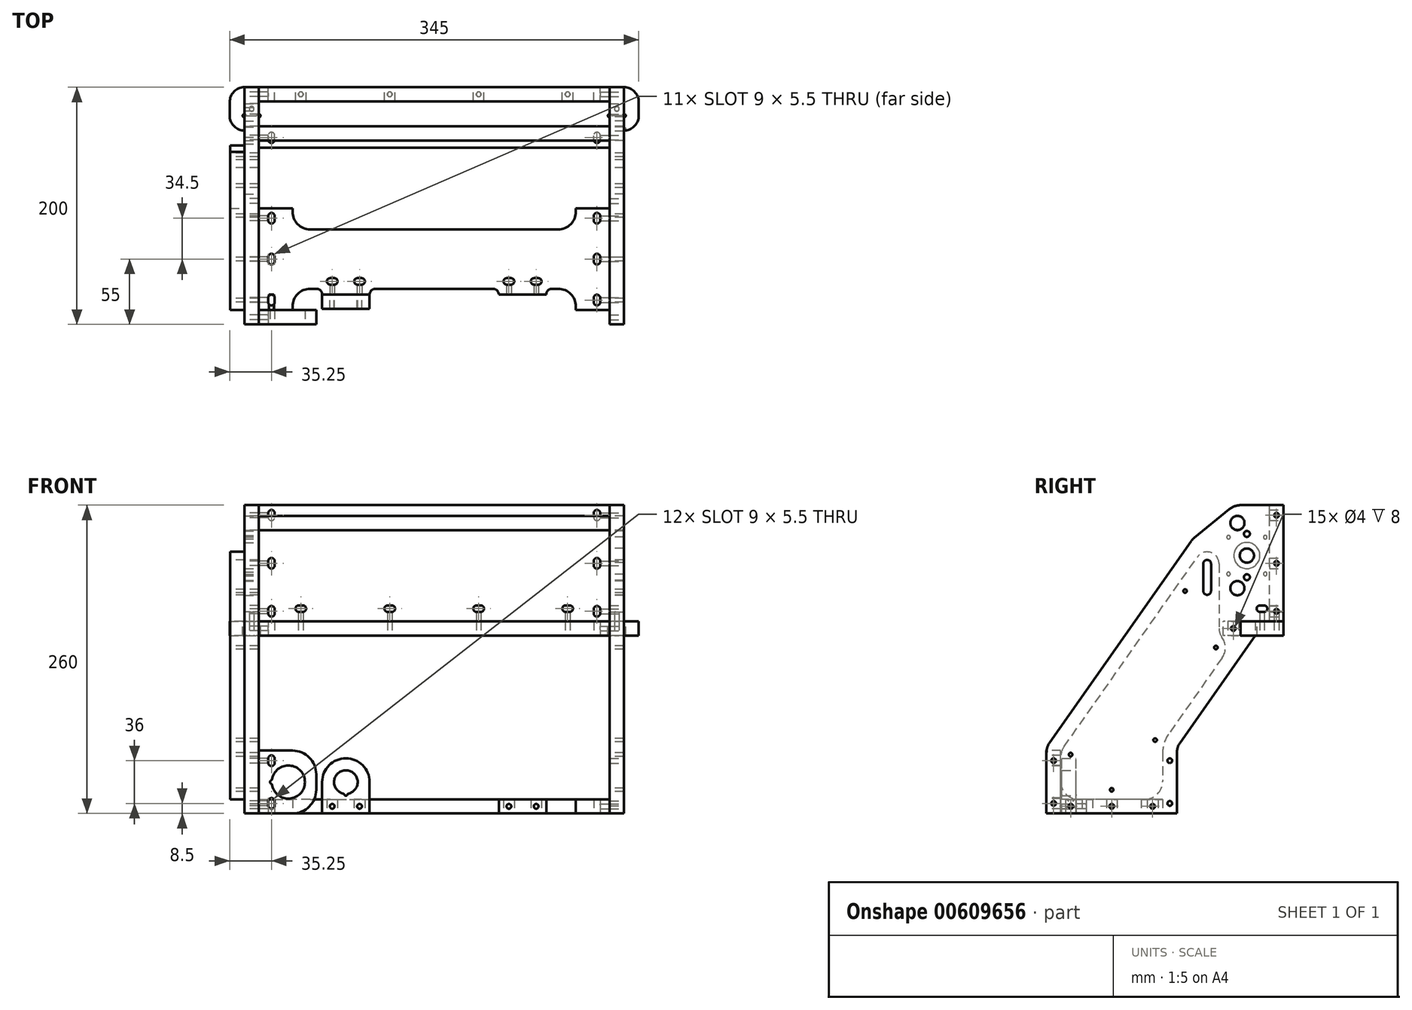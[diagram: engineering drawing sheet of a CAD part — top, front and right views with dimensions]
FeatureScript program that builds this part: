
annotation { "Feature Type Name" : "Feature", "Feature Type Description" : "" }
export const myFeature = defineFeature(function(context is Context, id is Id, definition is map)
    precondition{}
    {
        {
            var Q0;
            Q0=qCreatedBy(makeId("Front.planeOp"),FACE);
            var sketch = newSketch(context, id + "F0", { "sketchPlane" : qUnion([Q0])});
            skLineSegment(sketch, "E0.bottom", {"start": v(-148, 0) * mm, "end": v(148, 0) * mm});
            skLineSegment(sketch, "E0.top", {"start": v(-148, 98) * mm, "end": v(148, 98) * mm});
            skLineSegment(sketch, "E0.left", {"start": v(-148, 0) * mm, "end": v(-148, 98) * mm});
            skLineSegment(sketch, "E0.right", {"start": v(148, 0) * mm, "end": v(148, 98) * mm});
            skSolve(sketch);
        }
        {
            var Q0;
            Q0=qSketchRegion(id+"F0",true);
            extrude(context, id + "F1", {"entities" : qUnion([Q0]), "depth" : 12 * mm, "offsetDistance" : 25 * mm});
        }
        {
            var Q0;
            Q0=makeQuery(id+"F1.opExtrude","SWEPT_FACE",FACE,{"disambiguationData":[OSD([sQuery(id+"F0.wireOp",EDGE,"E0.left")])]});
            var sketch = newSketch(context, id + "F2", { "sketchPlane" : qUnion([Q0])});
            skLineSegment(sketch, "E1.bottom", {"start": v(0, 98) * mm, "end": v(56.7, 98) * mm});
            skLineSegment(sketch, "E1.top", {"start": v(90, -162) * mm, "end": v(200, -162) * mm});
            skLineSegment(sketch, "E1.right", {"start": v(56.7, 98) * mm, "end": v(200, -105.92) * mm});
            skLineSegment(sketch, "E2", {"start": v(200, -162) * mm, "end": v(200, -105.92) * mm});
            skLineSegment(sketch, "E3", {"start": v(24, -12) * mm, "end": v(90, -105.92) * mm});
            skLineSegment(sketch, "E4", {"start": v(0, 0) * mm, "end": v(0, 98) * mm});
            skLineSegment(sketch, "E5", {"start": v(90, -162) * mm, "end": v(90, -105.92) * mm});
            skLineSegment(sketch, "E6", {"start": v(0, 0) * mm, "end": v(24, 0) * mm});
            skLineSegment(sketch, "E7", {"start": v(24, 0) * mm, "end": v(24, -12) * mm});
            skSolve(sketch);
        }
        {
            var Q0;
            Q0=qSketchRegion(id+"F2",true);
            extrude(context, id + "F3", {"entities" : qUnion([Q0]), "depth" : 12 * mm, "offsetDistance" : 25 * mm});
        }
        {
            var Q0;
            Q0=makeQuery(id+"F3.opExtrude","CAP_FACE",FACE,{"disambiguationData":[OSD([sQuery(id+"F2.wireOp",EDGE,"E1.bottom"),sQuery(id+"F2.wireOp",EDGE,"E1.top"),sQuery(id+"F2.wireOp",EDGE,"E1.left"),sQuery(id+"F2.wireOp",EDGE,"E1.right"),sQuery(id+"F2.wireOp",EDGE,"E2"),sQuery(id+"F2.wireOp",EDGE,"2146645f-f5f1-4766-9391-dd441536dbd0.filletArc"),sQuery(id+"F2.wireOp",EDGE,"94e26631-0c9e-45e8-bca5-160914bd0a3d.filletArc")])],"isStart":true});
            var sketch = newSketch(context, id + "F4", { "sketchPlane" : qUnion([Q0])});
            skCircle(sketch, "E8", {"center": v(-39, 28) * mm, "radius": 5.97 * mm});
            skCircle(sketch, "E9", {"center": v(-39, 83) * mm, "radius": 5.97 * mm});
            skLineSegment(sketch, "E10", {"start": v(-39, 28) * mm, "end": v(-39, 83) * mm, "construction": true});
            skCircle(sketch, "E11", {"center": v(-31, 55.5) * mm, "radius": 11 * mm});
            skPoint(sketch, "E11.centerSnap0", {"position": v(-39, 55.5) * mm});
            skLineSegment(sketch, "E12.bottom", {"start": v(-15.5, 71) * mm, "end": v(-46.5, 71) * mm, "construction": true});
            skLineSegment(sketch, "E12.top", {"start": v(-15.5, 40) * mm, "end": v(-46.5, 40) * mm, "construction": true});
            skLineSegment(sketch, "E12.left", {"start": v(-15.5, 71) * mm, "end": v(-15.5, 40) * mm, "construction": true});
            skLineSegment(sketch, "E12.right", {"start": v(-46.5, 71) * mm, "end": v(-46.5, 40) * mm, "construction": true});
            skLineSegment(sketch, "E13", {"start": v(-31, 55.5) * mm, "end": v(-31, 71) * mm, "construction": true});
            skLineSegment(sketch, "E14", {"start": v(-15.5, 55.5) * mm, "end": v(-31, 55.5) * mm, "construction": true});
            skCircle(sketch, "E15", {"center": v(-46.5, 71) * mm, "radius": 1.5 * mm});
            skCircle(sketch, "E16.1.0", {"center": v(-46.5, 40) * mm, "radius": 1.5 * mm});
            skCircle(sketch, "E16.2.0", {"center": v(-15.5, 40) * mm, "radius": 1.5 * mm});
            skCircle(sketch, "E16.3.0", {"center": v(-15.5, 71) * mm, "radius": 1.5 * mm});
            skCircle(sketch, "E17", {"center": v(-31, 73.75) * mm, "radius": 2.5 * mm});
            skCircle(sketch, "E18.MirrorC", {"center": v(-31, 37.25) * mm, "radius": 2.5 * mm});
            skSolve(sketch);
        }
        {
            var Q0;
            Q0=qSketchRegion(id+"F4",true);
            extrude(context, id + "F5", {"entities" : qUnion([Q0]), "operationType" : NewBodyOperationType.REMOVE, "oppositeDirection" : true, "depth" : 25 * mm, "offsetDistance" : 25 * mm});
        }
        {
            var Q0;
            Q0=makeQuery(id+"F3.opExtrude","CAP_FACE",FACE,{"disambiguationData":[OSD([sQuery(id+"F2.wireOp",EDGE,"E1.bottom"),sQuery(id+"F2.wireOp",EDGE,"E1.top"),sQuery(id+"F2.wireOp",EDGE,"E1.left"),sQuery(id+"F2.wireOp",EDGE,"E1.right"),sQuery(id+"F2.wireOp",EDGE,"E2"),sQuery(id+"F2.wireOp",EDGE,"2146645f-f5f1-4766-9391-dd441536dbd0.filletArc"),sQuery(id+"F2.wireOp",EDGE,"94e26631-0c9e-45e8-bca5-160914bd0a3d.filletArc")])],"isStart":false});
            var sketch = newSketch(context, id + "F6", { "sketchPlane" : qUnion([Q0])});
            skCircle(sketch, "E19", {"center": v(39, 83) * mm, "radius": 6 * mm});
            skSolve(sketch);
        }
        {
            var Q0;
            Q0=qSketchRegion(id+"F6",true);
            extrude(context, id + "F7", {"entities" : qUnion([Q0]), "oppositeDirection" : true, "depth" : 320 * mm, "offsetDistance" : 25 * mm});
        }
        {
            var Q0;
            Q0=makeQuery(id+"F1.opExtrude","SWEPT_FACE",FACE,{"disambiguationData":[OSD([sQuery(id+"F0.wireOp",EDGE,"E0.right")])]});
            var sketch = newSketch(context, id + "F8", { "sketchPlane" : qUnion([Q0])});
            skCircle(sketch, "E20.0", {"center": v(-39, 83) * mm, "radius": 5.97 * mm});
            skCircle(sketch, "E21.0", {"center": v(-39, 28) * mm, "radius": 5.97 * mm});
            skLineSegment(sketch, "E22.1", {"start": v(-90, -105.92) * mm, "end": v(-24, -12) * mm});
            skLineSegment(sketch, "E22.5", {"start": v(0, 98) * mm, "end": v(-56.7, 98) * mm});
            skLineSegment(sketch, "E22.6", {"start": v(-56.7, 98) * mm, "end": v(-200, -105.92) * mm});
            skLineSegment(sketch, "E22.8", {"start": v(0, 0) * mm, "end": v(0, 98) * mm});
            skLineSegment(sketch, "E22.9", {"start": v(-200, -105.92) * mm, "end": v(-200, -162) * mm});
            skLineSegment(sketch, "E22.10", {"start": v(-200, -162) * mm, "end": v(-90, -162) * mm});
            skLineSegment(sketch, "E22.11", {"start": v(-90, -162) * mm, "end": v(-90, -105.92) * mm});
            skCircle(sketch, "E23.0", {"center": v(-31, 73.75) * mm, "radius": 2.5 * mm});
            skCircle(sketch, "E24.0", {"center": v(-31, 37.25) * mm, "radius": 2.5 * mm});
            skCircle(sketch, "E25.0", {"center": v(-31, 55.5) * mm, "radius": 6 * mm});
            skLineSegment(sketch, "E26", {"start": v(-24, -12) * mm, "end": v(-24, 0) * mm});
            skLineSegment(sketch, "E27", {"start": v(-24, 0) * mm, "end": v(0, 0) * mm});
            skSolve(sketch);
        }
        {
            var Q0;
            Q0=qSketchRegion(id+"F8",true);
            extrude(context, id + "F9", {"entities" : qUnion([Q0]), "depth" : 12 * mm, "offsetDistance" : 25 * mm});
        }
        {
            var Q0;
            Q0=makeQuery(id+"F3.opExtrude","SWEPT_FACE",FACE,{"disambiguationData":[OSD([sQuery(id+"F2.wireOp",EDGE,"E2")])]});
            var sketch = newSketch(context, id + "F10", { "sketchPlane" : qUnion([Q0])});
            skLineSegment(sketch, "E28.bottom", {"start": v(-148, -162) * mm, "end": v(-119.5, -162) * mm});
            skLineSegment(sketch, "E28.top", {"start": v(-148, -109) * mm, "end": v(-119.5, -109) * mm});
            skLineSegment(sketch, "E28.left", {"start": v(-148, -162) * mm, "end": v(-148, -109) * mm});
            skLineSegment(sketch, "E28.right", {"start": v(-99.5, -142) * mm, "end": v(-99.5, -129) * mm});
            skArc(sketch, "E29", {"start": v(-136.8, -137.7) * mm, "mid": v(-109.02, -135.5) * mm, "end": v(-136.8, -133.3) * mm});
            skPoint(sketch, "E29.centerSnap0", {"position": v(-148, -135.5) * mm});
            skPoint(sketch, "E29.centerSnap1", {"position": v(-123, -160.5) * mm});
            skArc(sketch, "E30.filletArc", {"start": v(-99.5, -129) * mm, "mid": v(-105.36, -114.86) * mm, "end": v(-119.5, -109) * mm});
            skArc(sketch, "E31.filletArc", {"start": v(-119.5, -162) * mm, "mid": v(-105.36, -156.14) * mm, "end": v(-99.5, -142) * mm});
            skArc(sketch, "E32", {"start": v(-137.46, -134.08) * mm, "mid": v(-138.47, -135.5) * mm, "end": v(-137.46, -136.92) * mm});
            skPoint(sketch, "E33.visualSharp", {"position": v(-136.9, -134) * mm});
            skArc(sketch, "E33.filletArc", {"start": v(-137.46, -134.08) * mm, "mid": v(-137.02, -133.78) * mm, "end": v(-136.8, -133.3) * mm});
            skPoint(sketch, "E34.visualSharp", {"position": v(-136.9, -137) * mm});
            skArc(sketch, "E34.filletArc", {"start": v(-136.8, -137.7) * mm, "mid": v(-137.02, -137.22) * mm, "end": v(-137.46, -136.92) * mm});
            skSolve(sketch);
        }
        {
            var Q0;
            Q0=qSketchRegion(id+"F10",true);
            extrude(context, id + "F11", {"entities" : qUnion([Q0]), "oppositeDirection" : true, "depth" : 12 * mm, "offsetDistance" : 25 * mm});
        }
        {
            var Q0;
            Q0=makeQuery(id+"F3.opExtrude","SWEPT_FACE",FACE,{"disambiguationData":[OSD([sQuery(id+"F2.wireOp",EDGE,"E1.top")])]});
            var sketch = newSketch(context, id + "F12", { "sketchPlane" : qUnion([Q0])});
            skLineSegment(sketch, "E35.bottom", {"start": v(-104.5, 170) * mm, "end": v(-99.5, 170) * mm});
            skLineSegment(sketch, "E35.top", {"start": v(-148, 145) * mm, "end": v(148, 145) * mm, "construction": true});
            skLineSegment(sketch, "E36.top", {"start": v(-148, 188) * mm, "end": v(-119.5, 188) * mm});
            skPoint(sketch, "E37", {"position": v(-148, 145) * mm});
            skLineSegment(sketch, "E38.trimOffspring", {"start": v(-119.5, 185) * mm, "end": v(-119.5, 188) * mm});
            skPoint(sketch, "E39.visualSharp", {"position": v(-119.5, 170) * mm});
            skArc(sketch, "E39.filletArc", {"start": v(-119.5, 185) * mm, "mid": v(-115.1, 174.4) * mm, "end": v(-104.5, 170) * mm});
            skLineSegment(sketch, "E40", {"start": v(-148, 188) * mm, "end": v(-148, 145) * mm});
            skLineSegment(sketch, "E41", {"start": v(0, 145) * mm, "end": v(0, 170) * mm, "construction": true});
            skLineSegment(sketch, "E42.MirrorCS", {"start": v(104.5, 170) * mm, "end": v(99.5, 170) * mm});
            skArc(sketch, "E43.MirrorCS", {"start": v(119.5, 185) * mm, "mid": v(115.1, 174.4) * mm, "end": v(104.5, 170) * mm});
            skLineSegment(sketch, "E44.MirrorCS", {"start": v(119.5, 185) * mm, "end": v(119.5, 188) * mm});
            skLineSegment(sketch, "E45.MirrorCS", {"start": v(148, 188) * mm, "end": v(119.5, 188) * mm});
            skLineSegment(sketch, "E46.MirrorCS", {"start": v(148, 188) * mm, "end": v(148, 145) * mm});
            skLineSegment(sketch, "E47.MirrorCS", {"start": v(-119.5, 105) * mm, "end": v(-119.5, 102) * mm});
            skLineSegment(sketch, "E48.MirrorCS", {"start": v(119.5, 105) * mm, "end": v(119.5, 102) * mm});
            skLineSegment(sketch, "E49.MirrorCS", {"start": v(-148, 102) * mm, "end": v(-119.5, 102) * mm});
            skLineSegment(sketch, "E50.MirrorCS", {"start": v(148, 102) * mm, "end": v(119.5, 102) * mm});
            skLineSegment(sketch, "E51.MirrorCS", {"start": v(148, 102) * mm, "end": v(148, 145) * mm});
            skLineSegment(sketch, "E52.MirrorCS", {"start": v(-104.5, 120) * mm, "end": v(0, 120) * mm});
            skArc(sketch, "E53.MirrorCS", {"start": v(119.5, 105) * mm, "mid": v(115.1, 115.6) * mm, "end": v(104.5, 120) * mm});
            skLineSegment(sketch, "E54.MirrorCS", {"start": v(104.5, 120) * mm, "end": v(0, 120) * mm});
            skPoint(sketch, "E55.MirrorP", {"position": v(-119.5, 120) * mm});
            skArc(sketch, "E56.MirrorCS", {"start": v(-119.5, 105) * mm, "mid": v(-115.1, 115.6) * mm, "end": v(-104.5, 120) * mm});
            skLineSegment(sketch, "E57.MirrorCS", {"start": v(-148, 102) * mm, "end": v(-148, 145) * mm});
            skLineSegment(sketch, "E58", {"start": v(-137.25, 108.75) * mm, "end": v(-137.25, 112.25) * mm, "construction": true});
            skArc(sketch, "E59.0.startCap", {"start": v(-134.5, 108.75) * mm, "mid": v(-137.25, 106) * mm, "end": v(-140, 108.75) * mm});
            skArc(sketch, "E59.0.endCap", {"start": v(-140, 112.25) * mm, "mid": v(-137.25, 115) * mm, "end": v(-134.5, 112.25) * mm});
            skLineSegment(sketch, "E59.0.left", {"start": v(-140, 108.75) * mm, "end": v(-140, 112.25) * mm});
            skLineSegment(sketch, "E59.0.right", {"start": v(-134.5, 108.75) * mm, "end": v(-134.5, 112.25) * mm});
            skArc(sketch, "E60.MirrorCS", {"start": v(-140, 177.75) * mm, "mid": v(-137.25, 175) * mm, "end": v(-134.5, 177.75) * mm});
            skLineSegment(sketch, "E61.MirrorCS", {"start": v(-134.5, 181.25) * mm, "end": v(-134.5, 177.75) * mm});
            skArc(sketch, "E62.MirrorCS", {"start": v(-140, 181.25) * mm, "mid": v(-137.25, 184) * mm, "end": v(-134.5, 181.25) * mm});
            skLineSegment(sketch, "E63.MirrorCS", {"start": v(-140, 181.25) * mm, "end": v(-140, 177.75) * mm});
            skLineSegment(sketch, "E64", {"start": v(-137.25, 143.25) * mm, "end": v(-137.25, 146.75) * mm, "construction": true});
            skArc(sketch, "E65.0.startCap", {"start": v(-134.5, 143.25) * mm, "mid": v(-137.25, 140.5) * mm, "end": v(-140, 143.25) * mm});
            skArc(sketch, "E65.0.endCap", {"start": v(-140, 146.75) * mm, "mid": v(-137.25, 149.5) * mm, "end": v(-134.5, 146.75) * mm});
            skLineSegment(sketch, "E65.0.left", {"start": v(-140, 143.25) * mm, "end": v(-140, 146.75) * mm});
            skLineSegment(sketch, "E65.0.right", {"start": v(-134.5, 143.25) * mm, "end": v(-134.5, 146.75) * mm});
            skPoint(sketch, "E66", {"position": v(-137.25, 145) * mm});
            skLineSegment(sketch, "E67.MirrorCS", {"start": v(137.25, 108.75) * mm, "end": v(137.25, 112.25) * mm, "construction": true});
            skLineSegment(sketch, "E68.MirrorCS", {"start": v(137.25, 143.25) * mm, "end": v(137.25, 146.75) * mm, "construction": true});
            skLineSegment(sketch, "E69.MirrorCS", {"start": v(134.5, 108.75) * mm, "end": v(134.5, 112.25) * mm});
            skPoint(sketch, "E70.MirrorP", {"position": v(137.25, 145) * mm});
            skLineSegment(sketch, "E71.MirrorCS", {"start": v(140, 181.25) * mm, "end": v(140, 177.75) * mm});
            skLineSegment(sketch, "E72.MirrorCS", {"start": v(140, 143.25) * mm, "end": v(140, 146.75) * mm});
            skLineSegment(sketch, "E73.MirrorCS", {"start": v(134.5, 181.25) * mm, "end": v(134.5, 177.75) * mm});
            skLineSegment(sketch, "E74.MirrorCS", {"start": v(140, 108.75) * mm, "end": v(140, 112.25) * mm});
            skLineSegment(sketch, "E75.MirrorCS", {"start": v(134.5, 143.25) * mm, "end": v(134.5, 146.75) * mm});
            skArc(sketch, "E76.MirrorCS", {"start": v(140, 112.25) * mm, "mid": v(137.25, 115) * mm, "end": v(134.5, 112.25) * mm});
            skArc(sketch, "E77.MirrorCS", {"start": v(140, 181.25) * mm, "mid": v(137.25, 184) * mm, "end": v(134.5, 181.25) * mm});
            skArc(sketch, "E78.MirrorCS", {"start": v(134.5, 108.75) * mm, "mid": v(137.25, 106) * mm, "end": v(140, 108.75) * mm});
            skArc(sketch, "E79.MirrorCS", {"start": v(140, 146.75) * mm, "mid": v(137.25, 149.5) * mm, "end": v(134.5, 146.75) * mm});
            skPoint(sketch, "E80.MirrorP", {"position": v(119.5, 120) * mm});
            skArc(sketch, "E81.MirrorCS", {"start": v(140, 177.75) * mm, "mid": v(137.25, 175) * mm, "end": v(134.5, 177.75) * mm});
            skPoint(sketch, "E82.MirrorP", {"position": v(119.5, 170) * mm});
            skArc(sketch, "E83.MirrorCS", {"start": v(134.5, 143.25) * mm, "mid": v(137.25, 140.5) * mm, "end": v(140, 143.25) * mm});
            skLineSegment(sketch, "E84", {"start": v(-94.5, 175) * mm, "end": v(-54.5, 175) * mm});
            skArc(sketch, "E85", {"start": v(-99.5, 170) * mm, "mid": v(-95.96, 171.46) * mm, "end": v(-94.5, 175) * mm});
            skPoint(sketch, "E86.orphan", {"position": v(0, 170) * mm});
            skArc(sketch, "E87.MirrorCS", {"start": v(-49.5, 170) * mm, "mid": v(-53.04, 171.46) * mm, "end": v(-54.5, 175) * mm});
            skLineSegment(sketch, "E88", {"start": v(-49.5, 170) * mm, "end": v(0, 170) * mm});
            skLineSegment(sketch, "E89.MirrorCS", {"start": v(49.5, 170) * mm, "end": v(0, 170) * mm});
            skArc(sketch, "E90.MirrorCS", {"start": v(49.5, 170) * mm, "mid": v(53.04, 171.46) * mm, "end": v(54.5, 175) * mm});
            skLineSegment(sketch, "E91.MirrorCS", {"start": v(94.5, 175) * mm, "end": v(54.5, 175) * mm});
            skArc(sketch, "E92.MirrorCS", {"start": v(99.5, 170) * mm, "mid": v(95.96, 171.46) * mm, "end": v(94.5, 175) * mm});
            skLineSegment(sketch, "E93", {"start": v(-87.75, 163.75) * mm, "end": v(-84.25, 163.75) * mm, "construction": true});
            skArc(sketch, "E94.0.startCap", {"start": v(-87.75, 161) * mm, "mid": v(-90.5, 163.75) * mm, "end": v(-87.75, 166.5) * mm});
            skArc(sketch, "E94.0.endCap", {"start": v(-84.25, 166.5) * mm, "mid": v(-81.5, 163.75) * mm, "end": v(-84.25, 161) * mm});
            skLineSegment(sketch, "E94.0.left", {"start": v(-87.75, 166.5) * mm, "end": v(-84.25, 166.5) * mm});
            skLineSegment(sketch, "E94.0.right", {"start": v(-87.75, 161) * mm, "end": v(-84.25, 161) * mm});
            skLineSegment(sketch, "E95", {"start": v(-94.5, 175) * mm, "end": v(-94.5, 170) * mm, "construction": true});
            skLineSegment(sketch, "E96", {"start": v(-74.5, 175) * mm, "end": v(-74.5, 172.2) * mm, "construction": true});
            skArc(sketch, "E97.MirrorCS", {"start": v(-64.75, 166.5) * mm, "mid": v(-67.5, 163.75) * mm, "end": v(-64.75, 161) * mm});
            skLineSegment(sketch, "E98.MirrorCS", {"start": v(-61.25, 161) * mm, "end": v(-64.75, 161) * mm});
            skLineSegment(sketch, "E99.MirrorCS", {"start": v(-61.25, 166.5) * mm, "end": v(-64.75, 166.5) * mm});
            skArc(sketch, "E100.MirrorCS", {"start": v(-61.25, 161) * mm, "mid": v(-58.5, 163.75) * mm, "end": v(-61.25, 166.5) * mm});
            skLineSegment(sketch, "E101.MirrorCS", {"start": v(61.25, 166.5) * mm, "end": v(64.75, 166.5) * mm});
            skLineSegment(sketch, "E102.MirrorCS", {"start": v(87.75, 166.5) * mm, "end": v(84.25, 166.5) * mm});
            skArc(sketch, "E103.MirrorCS", {"start": v(61.25, 161) * mm, "mid": v(58.5, 163.75) * mm, "end": v(61.25, 166.5) * mm});
            skLineSegment(sketch, "E104.MirrorCS", {"start": v(61.25, 161) * mm, "end": v(64.75, 161) * mm});
            skArc(sketch, "E105.MirrorCS", {"start": v(64.75, 166.5) * mm, "mid": v(67.5, 163.75) * mm, "end": v(64.75, 161) * mm});
            skArc(sketch, "E106.MirrorCS", {"start": v(84.25, 166.5) * mm, "mid": v(81.5, 163.75) * mm, "end": v(84.25, 161) * mm});
            skLineSegment(sketch, "E107.MirrorCS", {"start": v(87.75, 161) * mm, "end": v(84.25, 161) * mm});
            skArc(sketch, "E108.MirrorCS", {"start": v(87.75, 161) * mm, "mid": v(90.5, 163.75) * mm, "end": v(87.75, 166.5) * mm});
            skSolve(sketch);
        }
        {
            var Q0;
            Q0=qSketchRegion(id+"F12",true);
            extrude(context, id + "F13", {"entities" : qUnion([Q0]), "oppositeDirection" : true, "depth" : 12 * mm, "offsetDistance" : 25 * mm});
        }
        {
            var Q0;
            Q0=makeQuery(id+"F11.opExtrude","CAP_FACE",FACE,{"disambiguationData":[OSD([sQuery(id+"F10.wireOp",EDGE,"E28.bottom"),sQuery(id+"F10.wireOp",EDGE,"E28.top"),sQuery(id+"F10.wireOp",EDGE,"E28.left"),sQuery(id+"F10.wireOp",EDGE,"E28.right"),sQuery(id+"F10.wireOp",EDGE,"E29"),sQuery(id+"F10.wireOp",EDGE,"E30.filletArc"),sQuery(id+"F10.wireOp",EDGE,"E31.filletArc")])],"isStart":true});
            var sketch = newSketch(context, id + "F14", { "sketchPlane" : qUnion([Q0])});
            skLineSegment(sketch, "E109", {"start": v(-137.25, -115.75) * mm, "end": v(-137.25, -119.25) * mm, "construction": true});
            skArc(sketch, "E110.0.startCap", {"start": v(-140, -115.75) * mm, "mid": v(-137.25, -113) * mm, "end": v(-134.5, -115.75) * mm});
            skArc(sketch, "E110.0.endCap", {"start": v(-134.5, -119.25) * mm, "mid": v(-137.25, -122) * mm, "end": v(-140, -119.25) * mm});
            skLineSegment(sketch, "E110.0.left", {"start": v(-134.5, -115.75) * mm, "end": v(-134.5, -119.25) * mm});
            skLineSegment(sketch, "E110.0.right", {"start": v(-140, -115.75) * mm, "end": v(-140, -119.25) * mm});
            skLineSegment(sketch, "E111", {"start": v(-148, -135.5) * mm, "end": v(-136.97, -135.5) * mm, "construction": true});
            skLineSegment(sketch, "E112.MirrorCS", {"start": v(-134.5, -155.25) * mm, "end": v(-134.5, -151.75) * mm});
            skLineSegment(sketch, "E113.MirrorCS", {"start": v(-140, -155.25) * mm, "end": v(-140, -151.75) * mm});
            skArc(sketch, "E114.MirrorCS", {"start": v(-140, -155.25) * mm, "mid": v(-137.25, -158) * mm, "end": v(-134.5, -155.25) * mm});
            skArc(sketch, "E115.MirrorCS", {"start": v(-134.5, -151.75) * mm, "mid": v(-137.25, -149) * mm, "end": v(-140, -151.75) * mm});
            skSolve(sketch);
        }
        {
            var Q0;
            Q0 = qSketchRegion(id + "F14", true);
            extrude(context, id + "F15", {"entities" : qUnion([Q0]), "operationType" : NewBodyOperationType.REMOVE, "oppositeDirection" : true, "depth" : 25 * mm, "offsetDistance" : 25 * mm});
        }
        {
            var Q0;
            Q0=makeQuery(id+"F1.opExtrude","SWEPT_FACE",FACE,{"disambiguationData":[OSD([sQuery(id+"F0.wireOp",EDGE,"E0.bottom")])]});
            var sketch = newSketch(context, id + "F16", { "sketchPlane" : qUnion([Q0])});
            skLineSegment(sketch, "E116", {"start": v(-160, 0) * mm, "end": v(160, 0) * mm});
            skLineSegment(sketch, "E117", {"start": v(-160, 0) * mm, "end": v(-160, 12.5) * mm});
            skLineSegment(sketch, "E118", {"start": v(-157.7, 24) * mm, "end": v(-150.3, 24) * mm});
            skLineSegment(sketch, "E119", {"start": v(-148, 26.3) * mm, "end": v(-148, 51) * mm});
            skLineSegment(sketch, "E120", {"start": v(-148, 51) * mm, "end": v(0, 51) * mm});
            skLineSegment(sketch, "E121", {"start": v(0, 51) * mm, "end": v(0, 0) * mm, "construction": true});
            skArc(sketch, "E122", {"start": v(-149.37, 23.4) * mm, "mid": v(-146.94, 22.94) * mm, "end": v(-147.4, 25.37) * mm});
            skArc(sketch, "E123.MirrorC", {"start": v(149.37, 23.4) * mm, "mid": v(146.94, 22.94) * mm, "end": v(147.4, 25.37) * mm});
            skLineSegment(sketch, "E124.MirrorCS", {"start": v(148, 51) * mm, "end": v(0, 51) * mm});
            skLineSegment(sketch, "E125.MirrorCS", {"start": v(148, 26.3) * mm, "end": v(148, 51) * mm});
            skLineSegment(sketch, "E126.MirrorCS", {"start": v(158.5, 24) * mm, "end": v(150.3, 24) * mm});
            skLineSegment(sketch, "E127.MirrorCS", {"start": v(160, 0) * mm, "end": v(160, 22.5) * mm});
            skPoint(sketch, "E128.visualSharp", {"position": v(149.5, 24) * mm});
            skArc(sketch, "E128.filletArc", {"start": v(150.3, 24) * mm, "mid": v(149.74, 23.84) * mm, "end": v(149.37, 23.4) * mm});
            skPoint(sketch, "E129.visualSharp", {"position": v(148, 25.5) * mm});
            skArc(sketch, "E129.filletArc", {"start": v(147.4, 25.37) * mm, "mid": v(147.84, 25.74) * mm, "end": v(148, 26.3) * mm});
            skPoint(sketch, "E130.visualSharp", {"position": v(-149.5, 24) * mm});
            skArc(sketch, "E130.filletArc", {"start": v(-149.37, 23.4) * mm, "mid": v(-149.74, 23.84) * mm, "end": v(-150.3, 24) * mm});
            skPoint(sketch, "E131.visualSharp", {"position": v(-148, 25.5) * mm});
            skArc(sketch, "E131.filletArc", {"start": v(-148, 26.3) * mm, "mid": v(-147.84, 25.74) * mm, "end": v(-147.4, 25.37) * mm});
            skArc(sketch, "E132", {"start": v(-161.16, 24.95) * mm, "mid": v(-172.49, 11.92) * mm, "end": v(-160, 0) * mm});
            skArc(sketch, "E133", {"start": v(-161.09, 36.45) * mm, "mid": v(-172.49, 23.46) * mm, "end": v(-160, 11.5) * mm});
            skLineSegment(sketch, "E134", {"start": v(-160, 26.3) * mm, "end": v(-160, 35.46) * mm});
            skArc(sketch, "E135", {"start": v(-160.6, 25.37) * mm, "mid": v(-161.06, 22.94) * mm, "end": v(-158.63, 23.4) * mm});
            skPoint(sketch, "E136.visualSharp", {"position": v(-160, 25.5) * mm});
            skArc(sketch, "E136.filletArc", {"start": v(-160.6, 25.37) * mm, "mid": v(-160.16, 25.74) * mm, "end": v(-160, 26.3) * mm});
            skPoint(sketch, "E137.visualSharp", {"position": v(-158.5, 24) * mm});
            skArc(sketch, "E137.filletArc", {"start": v(-157.7, 24) * mm, "mid": v(-158.26, 23.84) * mm, "end": v(-158.63, 23.4) * mm});
            skLineSegment(sketch, "E138", {"start": v(-172.5, 12.5) * mm, "end": v(-172.5, 24) * mm});
            skPoint(sketch, "E138.startSnap0", {"position": v(-172.5, 24) * mm});
            skPoint(sketch, "E139.visualSharp", {"position": v(-160, 36.5) * mm});
            skArc(sketch, "E139.filletArc", {"start": v(-160, 35.46) * mm, "mid": v(-160.32, 36.2) * mm, "end": v(-161.09, 36.45) * mm});
            skArc(sketch, "E140.MirrorCS", {"start": v(160.6, 25.37) * mm, "mid": v(160.16, 25.74) * mm, "end": v(160, 26.3) * mm});
            skArc(sketch, "E141.MirrorCS", {"start": v(160, 35.46) * mm, "mid": v(160.32, 36.2) * mm, "end": v(161.09, 36.45) * mm});
            skArc(sketch, "E142.MirrorCS", {"start": v(157.7, 24) * mm, "mid": v(158.26, 23.84) * mm, "end": v(158.63, 23.4) * mm});
            skArc(sketch, "E143.MirrorCS", {"start": v(160.6, 25.37) * mm, "mid": v(161.06, 22.94) * mm, "end": v(158.63, 23.4) * mm});
            skPoint(sketch, "E144.MirrorP", {"position": v(160, 36.5) * mm});
            skPoint(sketch, "E145.MirrorP", {"position": v(160, 25.5) * mm});
            skLineSegment(sketch, "E146.MirrorCS", {"start": v(172.5, 12.5) * mm, "end": v(172.5, 24) * mm});
            skArc(sketch, "E147.MirrorCS", {"start": v(161.09, 36.45) * mm, "mid": v(172.49, 23.46) * mm, "end": v(160, 11.5) * mm});
            skLineSegment(sketch, "E148.MirrorCS", {"start": v(160, 0) * mm, "end": v(160, 12.5) * mm});
            skLineSegment(sketch, "E149.MirrorCS", {"start": v(160, 26.3) * mm, "end": v(160, 35.46) * mm});
            skArc(sketch, "E150.MirrorCS", {"start": v(161.16, 24.95) * mm, "mid": v(172.49, 11.92) * mm, "end": v(160, 0) * mm});
            skPoint(sketch, "E151.MirrorP", {"position": v(172.5, 24) * mm});
            skPoint(sketch, "E152.MirrorP", {"position": v(158.5, 24) * mm});
            skSolve(sketch);
        }
        {
            var Q0;
            Q0 = qSketchRegion(id + "F16", true);
            extrude(context, id + "F17", {"entities" : qUnion([Q0]), "depth" : 12 * mm, "offsetDistance" : 25 * mm});
        }
        {
            var Q0;
            Q0=makeQuery(id+"F3.opExtrude","CAP_FACE",FACE,{"disambiguationData":[OSD([sQuery(id+"F2.wireOp",EDGE,"E1.bottom"),sQuery(id+"F2.wireOp",EDGE,"E1.top"),sQuery(id+"F2.wireOp",EDGE,"E1.right"),sQuery(id+"F2.wireOp",EDGE,"E2"),sQuery(id+"F2.wireOp",EDGE,"94e26631-0c9e-45e8-bca5-160914bd0a3d.filletArc"),sQuery(id+"F2.wireOp",EDGE,"E3"),sQuery(id+"F2.wireOp",EDGE,"E4"),sQuery(id+"F2.wireOp",EDGE,"3c304bfc-2885-443d-81d9-234e97ae9333.filletArc"),sQuery(id+"F2.wireOp",EDGE,"E5"),sQuery(id+"F2.wireOp",EDGE,"930fecb7-9af6-459d-8abb-d03ba6c7b7a5.filletArc"),sQuery(id+"F2.wireOp",EDGE,"yWCbbJBZ-1GEx-dhOH-k0kd-LSXJYkVx6NrP"),sQuery(id+"F2.wireOp",EDGE,"cebc93dc-49be-47df-9592-c98bafc6a396.filletArc"),sQuery(id+"F2.wireOp",EDGE,"0R2F742G-mTnw-hJEY-WdgB-tpz7tOERiha1"),sQuery(id+"F2.wireOp",EDGE,"3aeea579-ff88-4944-83f2-f3d4fbf2bd07.filletArc"),sQuery(id+"F2.wireOp",EDGE,"c7c51ab0-1a95-4586-bb57-7b3897809644.filletArc")])],"isStart":false});
            var sketch = newSketch(context, id + "F18", { "sketchPlane" : qUnion([Q0])});
            skCircle(sketch, "E153", {"center": v(194, -153.5) * mm, "radius": 2 * mm});
            skCircle(sketch, "E154", {"center": v(194, -117.5) * mm, "radius": 2 * mm});
            skLineSegment(sketch, "E155", {"start": v(145, -162) * mm, "end": v(145, -142.37) * mm, "construction": true});
            skCircle(sketch, "E156.MirrorC", {"center": v(96, -117.5) * mm, "radius": 2 * mm});
            skCircle(sketch, "E157.MirrorC", {"center": v(96, -153.5) * mm, "radius": 2 * mm});
            skCircle(sketch, "E158", {"center": v(179.5, -156) * mm, "radius": 2 * mm});
            skCircle(sketch, "E159", {"center": v(145, -156) * mm, "radius": 2 * mm});
            skCircle(sketch, "E160.MirrorC", {"center": v(110.5, -156) * mm, "radius": 2 * mm});
            skCircle(sketch, "E161", {"center": v(6, 89.5) * mm, "radius": 2 * mm});
            skCircle(sketch, "E162.0.1.0", {"center": v(6, 49) * mm, "radius": 2 * mm});
            skCircle(sketch, "E162.0.2.0", {"center": v(6, 8.5) * mm, "radius": 2 * mm});
            skLineSegment(sketch, "E162.direction1", {"start": v(6, 89.5) * mm, "end": v(31, 89.5) * mm, "construction": true});
            skLineSegment(sketch, "E162.direction2", {"start": v(6, 89.5) * mm, "end": v(6, 49) * mm, "construction": true});
            skLineSegment(sketch, "E163", {"start": v(16.5, 10.75) * mm, "end": v(20, 10.75) * mm, "construction": true});
            skArc(sketch, "E164.0.startCap", {"start": v(16.5, 8) * mm, "mid": v(13.75, 10.75) * mm, "end": v(16.5, 13.5) * mm});
            skArc(sketch, "E164.0.endCap", {"start": v(20, 13.5) * mm, "mid": v(22.75, 10.75) * mm, "end": v(20, 8) * mm});
            skLineSegment(sketch, "E164.0.left", {"start": v(16.5, 13.5) * mm, "end": v(20, 13.5) * mm});
            skLineSegment(sketch, "E164.0.right", {"start": v(16.5, 8) * mm, "end": v(20, 8) * mm});
            skPoint(sketch, "E165", {"position": v(18.25, 10.75) * mm});
            skCircle(sketch, "E166", {"center": v(42.5, -6) * mm, "radius": 2 * mm});
            skPoint(sketch, "E166.centerSnap0", {"position": v(24, -6) * mm});
            skLineSegment(sketch, "E167", {"start": v(24, -6) * mm, "end": v(51, -6) * mm, "construction": true});
            skSolve(sketch);
        }
        {
            var Q0;
            Q0 = qSketchRegion(id + "F18", true);
            extrude(context, id + "F19", {"entities" : qUnion([Q0]), "operationType" : NewBodyOperationType.REMOVE, "oppositeDirection" : true, "depth" : 21 * mm, "offsetDistance" : 25 * mm});
        }
        {
            var Q0;
            Q0=makeQuery(id+"F1.opExtrude","CAP_FACE",FACE,{"disambiguationData":[OSD([sQuery(id+"F0.wireOp",EDGE,"E0.bottom"),sQuery(id+"F0.wireOp",EDGE,"E0.top"),sQuery(id+"F0.wireOp",EDGE,"E0.left"),sQuery(id+"F0.wireOp",EDGE,"E0.right")])],"isStart":true});
            var sketch = newSketch(context, id + "F20", { "sketchPlane" : qUnion([Q0])});
            skLineSegment(sketch, "E168", {"start": v(137.25, 91.25) * mm, "end": v(137.25, 87.75) * mm, "construction": true});
            skArc(sketch, "E169.0.startCap", {"start": v(134.5, 91.25) * mm, "mid": v(137.25, 94) * mm, "end": v(140, 91.25) * mm});
            skArc(sketch, "E169.0.endCap", {"start": v(140, 87.75) * mm, "mid": v(137.25, 85) * mm, "end": v(134.5, 87.75) * mm});
            skLineSegment(sketch, "E169.0.left", {"start": v(140, 91.25) * mm, "end": v(140, 87.75) * mm});
            skLineSegment(sketch, "E169.0.right", {"start": v(134.5, 91.25) * mm, "end": v(134.5, 87.75) * mm});
            skArc(sketch, "E170.0.1.0", {"start": v(134.5, 50.75) * mm, "mid": v(137.25, 53.5) * mm, "end": v(140, 50.75) * mm});
            skLineSegment(sketch, "E170.0.1.1", {"start": v(140, 50.75) * mm, "end": v(140, 47.25) * mm});
            skArc(sketch, "E170.0.1.2", {"start": v(140, 47.25) * mm, "mid": v(137.25, 44.5) * mm, "end": v(134.5, 47.25) * mm});
            skLineSegment(sketch, "E170.0.1.3", {"start": v(134.5, 50.75) * mm, "end": v(134.5, 47.25) * mm});
            skArc(sketch, "E170.0.2.0", {"start": v(134.5, 10.25) * mm, "mid": v(137.25, 13) * mm, "end": v(140, 10.25) * mm});
            skLineSegment(sketch, "E170.0.2.1", {"start": v(140, 10.25) * mm, "end": v(140, 6.75) * mm});
            skArc(sketch, "E170.0.2.2", {"start": v(140, 6.75) * mm, "mid": v(137.25, 4) * mm, "end": v(134.5, 6.75) * mm});
            skLineSegment(sketch, "E170.0.2.3", {"start": v(134.5, 10.25) * mm, "end": v(134.5, 6.75) * mm});
            skLineSegment(sketch, "E170.direction1", {"start": v(134.5, 87.75) * mm, "end": v(159, 87.75) * mm, "construction": true});
            skLineSegment(sketch, "E170.direction2", {"start": v(134.5, 87.75) * mm, "end": v(134.5, 47.25) * mm, "construction": true});
            skLineSegment(sketch, "E171", {"start": v(0, 0) * mm, "end": v(0, 98) * mm, "construction": true});
            skLineSegment(sketch, "E172.MirrorCS", {"start": v(-134.5, 91.25) * mm, "end": v(-134.5, 87.75) * mm});
            skLineSegment(sketch, "E173.MirrorCS", {"start": v(-140, 91.25) * mm, "end": v(-140, 87.75) * mm});
            skLineSegment(sketch, "E174.MirrorCS", {"start": v(-134.5, 50.75) * mm, "end": v(-134.5, 47.25) * mm});
            skLineSegment(sketch, "E175.MirrorCS", {"start": v(-140, 50.75) * mm, "end": v(-140, 47.25) * mm});
            skLineSegment(sketch, "E176.MirrorCS", {"start": v(-140, 10.25) * mm, "end": v(-140, 6.75) * mm});
            skLineSegment(sketch, "E177.MirrorCS", {"start": v(-134.5, 10.25) * mm, "end": v(-134.5, 6.75) * mm});
            skArc(sketch, "E178.MirrorCS", {"start": v(-134.5, 91.25) * mm, "mid": v(-137.25, 94) * mm, "end": v(-140, 91.25) * mm});
            skArc(sketch, "E179.MirrorCS", {"start": v(-140, 87.75) * mm, "mid": v(-137.25, 85) * mm, "end": v(-134.5, 87.75) * mm});
            skArc(sketch, "E180.MirrorCS", {"start": v(-134.5, 50.75) * mm, "mid": v(-137.25, 53.5) * mm, "end": v(-140, 50.75) * mm});
            skArc(sketch, "E181.MirrorCS", {"start": v(-140, 47.25) * mm, "mid": v(-137.25, 44.5) * mm, "end": v(-134.5, 47.25) * mm});
            skArc(sketch, "E182.MirrorCS", {"start": v(-134.5, 10.25) * mm, "mid": v(-137.25, 13) * mm, "end": v(-140, 10.25) * mm});
            skArc(sketch, "E183.MirrorCS", {"start": v(-140, 6.75) * mm, "mid": v(-137.25, 4) * mm, "end": v(-134.5, 6.75) * mm});
            skLineSegment(sketch, "E184", {"start": v(-110.75, 10.75) * mm, "end": v(-114.25, 10.75) * mm, "construction": true});
            skArc(sketch, "E185.0.startCap", {"start": v(-110.75, 13.5) * mm, "mid": v(-108, 10.75) * mm, "end": v(-110.75, 8) * mm});
            skArc(sketch, "E185.0.endCap", {"start": v(-114.25, 8) * mm, "mid": v(-117, 10.75) * mm, "end": v(-114.25, 13.5) * mm});
            skLineSegment(sketch, "E185.0.left", {"start": v(-110.75, 8) * mm, "end": v(-114.25, 8) * mm});
            skLineSegment(sketch, "E185.0.right", {"start": v(-110.75, 13.5) * mm, "end": v(-114.25, 13.5) * mm});
            skArc(sketch, "E186.1.0.0", {"start": v(-39.25, 8) * mm, "mid": v(-42, 10.75) * mm, "end": v(-39.25, 13.5) * mm});
            skLineSegment(sketch, "E186.1.0.1", {"start": v(-35.75, 13.5) * mm, "end": v(-39.25, 13.5) * mm});
            skLineSegment(sketch, "E186.1.0.2", {"start": v(-35.75, 8) * mm, "end": v(-39.25, 8) * mm});
            skArc(sketch, "E186.1.0.3", {"start": v(-35.75, 13.5) * mm, "mid": v(-33, 10.75) * mm, "end": v(-35.75, 8) * mm});
            skArc(sketch, "E186.2.0.0", {"start": v(35.75, 8) * mm, "mid": v(33, 10.75) * mm, "end": v(35.75, 13.5) * mm});
            skLineSegment(sketch, "E186.2.0.1", {"start": v(39.25, 13.5) * mm, "end": v(35.75, 13.5) * mm});
            skLineSegment(sketch, "E186.2.0.2", {"start": v(39.25, 8) * mm, "end": v(35.75, 8) * mm});
            skArc(sketch, "E186.2.0.3", {"start": v(39.25, 13.5) * mm, "mid": v(42, 10.75) * mm, "end": v(39.25, 8) * mm});
            skArc(sketch, "E186.3.0.0", {"start": v(110.75, 8) * mm, "mid": v(108, 10.75) * mm, "end": v(110.75, 13.5) * mm});
            skLineSegment(sketch, "E186.3.0.1", {"start": v(114.25, 13.5) * mm, "end": v(110.75, 13.5) * mm});
            skLineSegment(sketch, "E186.3.0.2", {"start": v(114.25, 8) * mm, "end": v(110.75, 8) * mm});
            skArc(sketch, "E186.3.0.3", {"start": v(114.25, 13.5) * mm, "mid": v(117, 10.75) * mm, "end": v(114.25, 8) * mm});
            skLineSegment(sketch, "E186.direction1", {"start": v(-114.25, 8) * mm, "end": v(-39.25, 8) * mm, "construction": true});
            skPoint(sketch, "E187", {"position": v(-37.5, 13.5) * mm});
            skSolve(sketch);
        }
        {
            var Q0;
            Q0 = qSketchRegion(id + "F20", true);
            extrude(context, id + "F21", {"entities" : qUnion([Q0]), "operationType" : NewBodyOperationType.REMOVE, "oppositeDirection" : true, "depth" : 25 * mm, "offsetDistance" : 25 * mm});
        }
        {
            var Q0;
            Q0=makeQuery(id+"F9.opExtrude","CAP_FACE",FACE,{"disambiguationData":[OSD([sQuery(id+"F8.wireOp",EDGE,"E20.0"),sQuery(id+"F8.wireOp",EDGE,"E21.0"),sQuery(id+"F8.wireOp",EDGE,"E22.0"),sQuery(id+"F8.wireOp",EDGE,"E22.1"),sQuery(id+"F8.wireOp",EDGE,"E22.2"),sQuery(id+"F8.wireOp",EDGE,"E22.3"),sQuery(id+"F8.wireOp",EDGE,"E22.5"),sQuery(id+"F8.wireOp",EDGE,"E22.6"),sQuery(id+"F8.wireOp",EDGE,"E22.7"),sQuery(id+"F8.wireOp",EDGE,"E22.8"),sQuery(id+"F8.wireOp",EDGE,"E22.9"),sQuery(id+"F8.wireOp",EDGE,"E22.10"),sQuery(id+"F8.wireOp",EDGE,"E22.11"),sQuery(id+"F8.wireOp",EDGE,"E22.12"),sQuery(id+"F8.wireOp",EDGE,"0fa0f1f6-a39c-456d-a7d0-3881c9b7fbf4.0"),sQuery(id+"F8.wireOp",EDGE,"0fa0f1f6-a39c-456d-a7d0-3881c9b7fbf4.2"),sQuery(id+"F8.wireOp",EDGE,"E23.0"),sQuery(id+"F8.wireOp",EDGE,"E24.0"),sQuery(id+"F8.wireOp",EDGE,"E25.0")])],"isStart":false});
            var sketch = newSketch(context, id + "F22", { "sketchPlane" : qUnion([Q0])});
            skCircle(sketch, "E188.0", {"center": v(-96, -117.5) * mm, "radius": 2 * mm});
            skCircle(sketch, "E189.0", {"center": v(-96, -153.5) * mm, "radius": 2 * mm});
            skCircle(sketch, "E190.0", {"center": v(-110.5, -156) * mm, "radius": 2 * mm});
            skCircle(sketch, "E191.0", {"center": v(-145, -156) * mm, "radius": 2 * mm});
            skCircle(sketch, "E192.0", {"center": v(-179.5, -156) * mm, "radius": 2 * mm});
            skCircle(sketch, "E193.0", {"center": v(-194, -153.5) * mm, "radius": 2 * mm});
            skCircle(sketch, "E194.0", {"center": v(-194, -117.5) * mm, "radius": 2 * mm});
            skCircle(sketch, "E195.0", {"center": v(-6, 8.5) * mm, "radius": 2 * mm});
            skCircle(sketch, "E196.0", {"center": v(-6, 49) * mm, "radius": 2 * mm});
            skCircle(sketch, "E197.0", {"center": v(-6, 89.5) * mm, "radius": 2 * mm});
            skCircle(sketch, "E198.0", {"center": v(-42.5, -6) * mm, "radius": 2 * mm});
            skLineSegment(sketch, "E199.0", {"start": v(-16.5, 8) * mm, "end": v(-20, 8) * mm});
            skArc(sketch, "E199.1", {"start": v(-16.5, 8) * mm, "mid": v(-13.75, 10.75) * mm, "end": v(-16.5, 13.5) * mm});
            skLineSegment(sketch, "E199.2", {"start": v(-16.5, 13.5) * mm, "end": v(-20, 13.5) * mm});
            skArc(sketch, "E199.3", {"start": v(-20, 13.5) * mm, "mid": v(-22.75, 10.75) * mm, "end": v(-20, 8) * mm});
            skSolve(sketch);
        }
        {
            var Q0;
            Q0 = qSketchRegion(id + "F22", true);
            extrude(context, id + "F23", {"entities" : qUnion([Q0]), "operationType" : NewBodyOperationType.REMOVE, "oppositeDirection" : true, "depth" : 21 * mm, "offsetDistance" : 25 * mm});
        }
        {
            var Q0;
            Q0=makeQuery(id+"F3.opExtrude","SWEPT_EDGE",EDGE,{"disambiguationData":[OSD([sQuery(id+"F2.wireOp",EDGE,"E1.bottom"),sQuery(id+"F2.wireOp",EDGE,"E1.right")])]});
            chamfer(context, id + "F24", {"entities" : qUnion([Q0]), "chamferType" : ChamferType.TWO_OFFSETS, "width1" : 15 * mm, "oppositeDirection" : false, "width2" : 35 * mm, "tangentPropagation" : true});
        }
        {
            var Q0;
            Q0=makeQuery(id+"F9.opExtrude","SWEPT_EDGE",EDGE,{"disambiguationData":[OSD([sQuery(id+"F8.wireOp",EDGE,"E22.5"),sQuery(id+"F8.wireOp",EDGE,"E22.6")])]});
            chamfer(context, id + "F25", {"entities" : qUnion([Q0]), "chamferType" : ChamferType.TWO_OFFSETS, "width1" : 35 * mm, "oppositeDirection" : false, "width2" : 15 * mm, "tangentPropagation" : true});
        }
        {
            var Q0;
            Q0=makeQuery(id+"F3.opExtrude","SWEPT_EDGE",EDGE,{"disambiguationData":[OSD([sQuery(id+"F2.wireOp",EDGE,"E1.right"),sQuery(id+"F2.wireOp",EDGE,"E2")])]});
            var Q1;
            Q1=makeQuery(id+"F9.opExtrude","SWEPT_EDGE",EDGE,{"disambiguationData":[OSD([sQuery(id+"F8.wireOp",EDGE,"E22.6"),sQuery(id+"F8.wireOp",EDGE,"E22.9")])]});
            var Q2;
            Q2=makeQuery(id+"F3.opExtrude","SWEPT_EDGE",EDGE,{"disambiguationData":[OSD([sQuery(id+"F2.wireOp",EDGE,"E3"),sQuery(id+"F2.wireOp",EDGE,"E5")])]});
            var Q3;
            Q3=makeQuery(id+"F9.opExtrude","SWEPT_EDGE",EDGE,{"disambiguationData":[OSD([sQuery(id+"F8.wireOp",EDGE,"E22.1"),sQuery(id+"F8.wireOp",EDGE,"E22.11")])]});
            var Q4;
            {var subQ0=sQuery(id+"F2.wireOp",EDGE,"E1.bottom");Q4=makeQuery(id+"F24.opChamfer","BLEND_EDGE",EDGE,{"blendedFrom":[makeQuery(id+"F3.opExtrude","SWEPT_EDGE",EDGE,{"disambiguationData":[OSD([subQ0,sQuery(id+"F2.wireOp",EDGE,"E1.right")])]}),makeQuery(id+"F3.opExtrude","SWEPT_FACE",FACE,{"disambiguationData":[OSD([subQ0])]})],"blendedInto":[makeQuery(id+"F3.opExtrude","SWEPT_FACE",FACE,{"disambiguationData":[OSD([subQ0])]})]});}
            var Q5;
            {var subQ0=sQuery(id+"F2.wireOp",EDGE,"E1.right");Q5=makeQuery(id+"F24.opChamfer","BLEND_EDGE",EDGE,{"blendedFrom":[makeQuery(id+"F3.opExtrude","SWEPT_EDGE",EDGE,{"disambiguationData":[OSD([sQuery(id+"F2.wireOp",EDGE,"E1.bottom"),subQ0])]}),makeQuery(id+"F3.opExtrude","SWEPT_FACE",FACE,{"disambiguationData":[OSD([subQ0])]})],"blendedInto":[makeQuery(id+"F3.opExtrude","SWEPT_FACE",FACE,{"disambiguationData":[OSD([subQ0])]})]});}
            var Q6;
            {var subQ0=sQuery(id+"F8.wireOp",EDGE,"E22.5");Q6=makeQuery(id+"F25.opChamfer","BLEND_EDGE",EDGE,{"blendedFrom":[makeQuery(id+"F9.opExtrude","SWEPT_EDGE",EDGE,{"disambiguationData":[OSD([subQ0,sQuery(id+"F8.wireOp",EDGE,"E22.6")])]}),makeQuery(id+"F9.opExtrude","SWEPT_FACE",FACE,{"disambiguationData":[OSD([subQ0])]})],"blendedInto":[makeQuery(id+"F9.opExtrude","SWEPT_FACE",FACE,{"disambiguationData":[OSD([subQ0])]})]});}
            var Q7;
            {var subQ0=sQuery(id+"F8.wireOp",EDGE,"E22.6");Q7=makeQuery(id+"F25.opChamfer","BLEND_EDGE",EDGE,{"blendedFrom":[makeQuery(id+"F9.opExtrude","SWEPT_EDGE",EDGE,{"disambiguationData":[OSD([sQuery(id+"F8.wireOp",EDGE,"E22.5"),subQ0])]}),makeQuery(id+"F9.opExtrude","SWEPT_FACE",FACE,{"disambiguationData":[OSD([subQ0])]})],"blendedInto":[makeQuery(id+"F9.opExtrude","SWEPT_FACE",FACE,{"disambiguationData":[OSD([subQ0])]})]});}
            fillet(context, id + "F26", {"entities" : qUnion([Q0, Q1, Q2, Q3, Q4, Q5, Q6, Q7]), "radius" : 15 * mm, "tangentPropagation" : true, "allowEdgeOverflow" : false});
        }
        {
            var Q0;
            Q0=makeQuery(id+"F17.opExtrude","CAP_FACE",FACE,{"disambiguationData":[OSD([sQuery(id+"F16.wireOp",EDGE,"E116"),sQuery(id+"F16.wireOp",EDGE,"E117"),sQuery(id+"F16.wireOp",EDGE,"E118"),sQuery(id+"F16.wireOp",EDGE,"E119"),sQuery(id+"F16.wireOp",EDGE,"E120"),sQuery(id+"F16.wireOp",EDGE,"E122"),sQuery(id+"F16.wireOp",EDGE,"E123.MirrorC"),sQuery(id+"F16.wireOp",EDGE,"E124.MirrorCS"),sQuery(id+"F16.wireOp",EDGE,"E125.MirrorCS"),sQuery(id+"F16.wireOp",EDGE,"E126.MirrorCS"),sQuery(id+"F16.wireOp",EDGE,"E127.MirrorCS")])],"isStart":false});
            var sketch = newSketch(context, id + "F27", { "sketchPlane" : qUnion([Q0])});
            skCircle(sketch, "E200", {"center": v(-154, 18.25) * mm, "radius": 2 * mm});
            skLineSegment(sketch, "E201", {"start": v(-137.25, 44.25) * mm, "end": v(-137.25, 40.75) * mm, "construction": true});
            skArc(sketch, "E202.0.startCap", {"start": v(-140, 44.25) * mm, "mid": v(-137.25, 47) * mm, "end": v(-134.5, 44.25) * mm});
            skArc(sketch, "E202.0.endCap", {"start": v(-134.5, 40.75) * mm, "mid": v(-137.25, 38) * mm, "end": v(-140, 40.75) * mm});
            skLineSegment(sketch, "E202.0.left", {"start": v(-134.5, 44.25) * mm, "end": v(-134.5, 40.75) * mm});
            skLineSegment(sketch, "E202.0.right", {"start": v(-140, 44.25) * mm, "end": v(-140, 40.75) * mm});
            skLineSegment(sketch, "E203", {"start": v(0, 0) * mm, "end": v(0, 51) * mm, "construction": true});
            skCircle(sketch, "E204.MirrorC", {"center": v(154, 18.25) * mm, "radius": 2 * mm});
            skLineSegment(sketch, "E205.MirrorCS", {"start": v(140, 44.25) * mm, "end": v(140, 40.75) * mm});
            skLineSegment(sketch, "E206.MirrorCS", {"start": v(134.5, 44.25) * mm, "end": v(134.5, 40.75) * mm});
            skArc(sketch, "E207.MirrorCS", {"start": v(134.5, 40.75) * mm, "mid": v(137.25, 38) * mm, "end": v(140, 40.75) * mm});
            skArc(sketch, "E208.MirrorCS", {"start": v(140, 44.25) * mm, "mid": v(137.25, 47) * mm, "end": v(134.5, 44.25) * mm});
            skCircle(sketch, "E209", {"center": v(-112.5, 6) * mm, "radius": 2 * mm});
            skCircle(sketch, "E210.1.0.0", {"center": v(-37.5, 6) * mm, "radius": 2 * mm});
            skCircle(sketch, "E210.2.0.0", {"center": v(37.5, 6) * mm, "radius": 2 * mm});
            skCircle(sketch, "E210.3.0.0", {"center": v(112.5, 6) * mm, "radius": 2 * mm});
            skLineSegment(sketch, "E210.direction1", {"start": v(-112.5, 6) * mm, "end": v(-37.5, 6) * mm, "construction": true});
            skSolve(sketch);
        }
        {
            var Q0;
            Q0 = qSketchRegion(id + "F27", true);
            extrude(context, id + "F28", {"entities" : qUnion([Q0]), "operationType" : NewBodyOperationType.REMOVE, "oppositeDirection" : true, "depth" : 21 * mm, "offsetDistance" : 25 * mm});
        }
        {
            var Q0;
            Q0=makeQuery(id+"F3.opExtrude","CAP_FACE",FACE,{"disambiguationData":[OSD([sQuery(id+"F2.wireOp",EDGE,"E1.bottom"),sQuery(id+"F2.wireOp",EDGE,"E1.top"),sQuery(id+"F2.wireOp",EDGE,"E1.right"),sQuery(id+"F2.wireOp",EDGE,"E2"),sQuery(id+"F2.wireOp",EDGE,"E3"),sQuery(id+"F2.wireOp",EDGE,"E4"),sQuery(id+"F2.wireOp",EDGE,"E5"),sQuery(id+"F2.wireOp",EDGE,"E6"),sQuery(id+"F2.wireOp",EDGE,"E7")])],"isStart":false});
            var sketch = newSketch(context, id + "F29", { "sketchPlane" : qUnion([Q0])});
            skLineSegment(sketch, "E211.1", {"start": v(188, -150) * mm, "end": v(188, -114.46) * mm});
            skLineSegment(sketch, "E211.2", {"start": v(102, -150) * mm, "end": v(188, -150) * mm});
            skLineSegment(sketch, "E211.10", {"start": v(185.27, -105.83) * mm, "end": v(72.68, 54.39) * mm});
            skLineSegment(sketch, "E211.11", {"start": v(42.88, -18) * mm, "end": v(97.1, -95.14) * mm});
            skArc(sketch, "E211.12", {"start": v(97.1, -95.14) * mm, "mid": v(100.74, -102.52) * mm, "end": v(102, -110.66) * mm});
            skLineSegment(sketch, "E211.13", {"start": v(102, -110.66) * mm, "end": v(102, -150) * mm});
            skArc(sketch, "E212.0", {"start": v(42.88, -18) * mm, "mid": v(51.12, -14.35) * mm, "end": v(54.5, -6) * mm});
            skLineSegment(sketch, "E213", {"start": v(54.5, 48.64) * mm, "end": v(54.5, -6) * mm});
            skArc(sketch, "E214.filletArc", {"start": v(72.68, 54.39) * mm, "mid": v(61.48, 58.17) * mm, "end": v(54.5, 48.64) * mm});
            skArc(sketch, "E215.filletArc", {"start": v(188, -114.46) * mm, "mid": v(187.3, -109.94) * mm, "end": v(185.27, -105.83) * mm});
            skSolve(sketch);
        }
        {
            var Q0;
            Q0 = qSketchRegion(id + "F29", true);
            extrude(context, id + "F30", {"entities" : qUnion([Q0]), "depth" : 12 * mm, "offsetDistance" : 25 * mm});
        }
        {
            var Q0;
            Q0=makeQuery(id+"F30.opExtrude","SWEPT_EDGE",EDGE,{"disambiguationData":[OSD([sQuery(id+"F29.wireOp",EDGE,"E211.11"),sQuery(id+"F29.wireOp",EDGE,"E212.0")])]});
            var Q1;
            Q1=makeQuery(id+"F30.opExtrude","SWEPT_EDGE",EDGE,{"disambiguationData":[OSD([sQuery(id+"F29.wireOp",EDGE,"E211.2"),sQuery(id+"F29.wireOp",EDGE,"E211.13")])]});
            var Q2;
            Q2=makeQuery(id+"F30.opExtrude","SWEPT_EDGE",EDGE,{"disambiguationData":[OSD([sQuery(id+"F29.wireOp",EDGE,"E211.1"),sQuery(id+"F29.wireOp",EDGE,"E211.2")])]});
            fillet(context, id + "F31", {"entities" : qUnion([Q0, Q1, Q2]), "radius" : 15 * mm, "tangentPropagation" : true, "allowEdgeOverflow" : false});
        }
        {
            var Q0;
            Q0=makeQuery(id+"F30.opExtrude","CAP_FACE",FACE,{"disambiguationData":[OSD([sQuery(id+"F29.wireOp",EDGE,"E211.1"),sQuery(id+"F29.wireOp",EDGE,"E211.2"),sQuery(id+"F29.wireOp",EDGE,"E211.10"),sQuery(id+"F29.wireOp",EDGE,"E211.11"),sQuery(id+"F29.wireOp",EDGE,"E211.12"),sQuery(id+"F29.wireOp",EDGE,"E211.13"),sQuery(id+"F29.wireOp",EDGE,"E212.0"),sQuery(id+"F29.wireOp",EDGE,"E213"),sQuery(id+"F29.wireOp",EDGE,"E214.filletArc"),sQuery(id+"F29.wireOp",EDGE,"E215.filletArc")])],"isStart":false});
            var sketch = newSketch(context, id + "F32", { "sketchPlane" : qUnion([Q0])});
            skLineSegment(sketch, "E216", {"start": v(64.5, 48.64) * mm, "end": v(64.5, 25.64) * mm, "construction": true});
            skArc(sketch, "E217.0.startCap", {"start": v(61.25, 48.64) * mm, "mid": v(64.5, 51.89) * mm, "end": v(67.75, 48.64) * mm});
            skArc(sketch, "E217.0.endCap", {"start": v(67.75, 25.64) * mm, "mid": v(64.5, 22.39) * mm, "end": v(61.25, 25.64) * mm});
            skLineSegment(sketch, "E217.0.left", {"start": v(67.75, 48.64) * mm, "end": v(67.75, 25.64) * mm});
            skLineSegment(sketch, "E217.0.right", {"start": v(61.25, 48.64) * mm, "end": v(61.25, 25.64) * mm});
            skCircle(sketch, "E218", {"center": v(57.14, -22.05) * mm, "radius": 1.5 * mm});
            skCircle(sketch, "E219", {"center": v(108.37, -100.11) * mm, "radius": 1.5 * mm});
            skCircle(sketch, "E220", {"center": v(145, -142) * mm, "radius": 1.5 * mm});
            skCircle(sketch, "E221", {"center": v(179.67, -112.35) * mm, "radius": 1.5 * mm});
            skCircle(sketch, "E222", {"center": v(83.1, 25.64) * mm, "radius": 1.5 * mm});
            skLineSegment(sketch, "E223.0", {"start": v(62.5, 48.64) * mm, "end": v(62.5, -6) * mm, "construction": true});
            skArc(sketch, "E223.1", {"start": v(66.14, 49.79) * mm, "mid": v(63.9, 50.54) * mm, "end": v(62.5, 48.64) * mm, "construction": true});
            skLineSegment(sketch, "E223.2", {"start": v(110, -110.66) * mm, "end": v(110, -135) * mm, "construction": true});
            skArc(sketch, "E223.3", {"start": v(103.64, -90.54) * mm, "mid": v(108.37, -100.11) * mm, "end": v(110, -110.66) * mm, "construction": true});
            skLineSegment(sketch, "E223.4", {"start": v(58.4, -26.18) * mm, "end": v(103.64, -90.54) * mm, "construction": true});
            skArc(sketch, "E223.5", {"start": v(58.53, -17.97) * mm, "mid": v(57.14, -22.05) * mm, "end": v(58.4, -26.18) * mm, "construction": true});
            skArc(sketch, "E223.6", {"start": v(110, -135) * mm, "mid": v(112.05, -139.95) * mm, "end": v(117, -142) * mm, "construction": true});
            skLineSegment(sketch, "E223.7", {"start": v(117, -142) * mm, "end": v(173, -142) * mm, "construction": true});
            skArc(sketch, "E223.8", {"start": v(62.5, -6) * mm, "mid": v(61.48, -12.3) * mm, "end": v(58.53, -17.97) * mm, "construction": true});
            skArc(sketch, "E223.9", {"start": v(173, -142) * mm, "mid": v(177.95, -139.95) * mm, "end": v(180, -135) * mm, "construction": true});
            skLineSegment(sketch, "E223.10", {"start": v(180, -135) * mm, "end": v(180, -114.46) * mm, "construction": true});
            skArc(sketch, "E223.11", {"start": v(180, -114.46) * mm, "mid": v(179.67, -112.35) * mm, "end": v(178.73, -110.43) * mm, "construction": true});
            skLineSegment(sketch, "E223.12", {"start": v(178.73, -110.43) * mm, "end": v(66.14, 49.79) * mm, "construction": true});
            skLineSegment(sketch, "E224", {"start": v(64.5, 25.64) * mm, "end": v(83.1, 25.64) * mm, "construction": true});
            skSolve(sketch);
        }
        {
            var Q0;
            Q0 = qSketchRegion(id + "F32", true);
            extrude(context, id + "F33", {"entities" : qUnion([Q0]), "operationType" : NewBodyOperationType.REMOVE, "endBound" : BoundingType.THROUGH_ALL, "oppositeDirection" : true, "depth" : 25 * mm, "offsetDistance" : 25 * mm});
        }
        {
            var Q0;
            Q0=makeQuery(id+"F13.opExtrude","SWEPT_FACE",FACE,{"disambiguationData":[OSD([sQuery(id+"F12.wireOp",EDGE,"E84"),sQuery(id+"F12.wireOp",EDGE,"5ef5005f-9529-4792-9d74-6e6948cf13f80.MirrorCS")])]});
            var sketch = newSketch(context, id + "F34", { "sketchPlane" : qUnion([Q0])});
            skLineSegment(sketch, "E225.left", {"start": v(-94.5, -162) * mm, "end": v(-94.5, -135.5) * mm});
            skLineSegment(sketch, "E225.right", {"start": v(-54.5, -162) * mm, "end": v(-54.5, -135.5) * mm});
            skPoint(sketch, "E226.visualSharp", {"position": v(-94.5, -115.02) * mm});
            skCircle(sketch, "E227", {"center": v(-86, -156) * mm, "radius": 2 * mm});
            skCircle(sketch, "E228", {"center": v(-63, -156) * mm, "radius": 2 * mm});
            skArc(sketch, "E229", {"start": v(-54.5, -135.5) * mm, "mid": v(-74.5, -115.5) * mm, "end": v(-94.5, -135.5) * mm});
            skPoint(sketch, "E229.centerSnap0", {"position": v(-74.5, -150) * mm});
            skLineSegment(sketch, "E230", {"start": v(-94.5, -162) * mm, "end": v(-54.5, -162) * mm});
            skArc(sketch, "E231", {"start": v(-72.33, -145.24) * mm, "mid": v(-74.5, -125.53) * mm, "end": v(-76.67, -145.24) * mm});
            skArc(sketch, "E232", {"start": v(-75.93, -145.92) * mm, "mid": v(-74.5, -146.98) * mm, "end": v(-73.07, -145.92) * mm});
            skPoint(sketch, "E233.visualSharp", {"position": v(-76, -145.36) * mm});
            skArc(sketch, "E233.filletArc", {"start": v(-75.93, -145.92) * mm, "mid": v(-76.21, -145.48) * mm, "end": v(-76.67, -145.24) * mm});
            skPoint(sketch, "E234.visualSharp", {"position": v(-73, -145.36) * mm});
            skArc(sketch, "E234.filletArc", {"start": v(-72.33, -145.24) * mm, "mid": v(-72.79, -145.48) * mm, "end": v(-73.07, -145.92) * mm});
            skSolve(sketch);
        }
        {
            var Q0;
            Q0 = qSketchRegion(id + "F34", true);
            extrude(context, id + "F35", {"entities" : qUnion([Q0]), "depth" : 12 * mm, "offsetDistance" : 25 * mm});
        }
        {
            var Q0;
            Q0=makeQuery(id+"F13.opExtrude","SWEPT_FACE",FACE,{"disambiguationData":[OSD([sQuery(id+"F12.wireOp",EDGE,"E91.MirrorCS")])]});
            var sketch = newSketch(context, id + "F36", { "sketchPlane" : qUnion([Q0])});
            skCircle(sketch, "E235.0", {"center": v(-86, -156) * mm, "radius": 2 * mm});
            skCircle(sketch, "E236.0", {"center": v(-63, -156) * mm, "radius": 2 * mm});
            skLineSegment(sketch, "E237", {"start": v(0, -165.2) * mm, "end": v(0, -150) * mm, "construction": true});
            skCircle(sketch, "E238.MirrorC", {"center": v(86, -156) * mm, "radius": 2 * mm});
            skCircle(sketch, "E239.MirrorC", {"center": v(63, -156) * mm, "radius": 2 * mm});
            skSolve(sketch);
        }
        {
            var Q0;
            Q0 = qSketchRegion(id + "F36", true);
            extrude(context, id + "F37", {"entities" : qUnion([Q0]), "operationType" : NewBodyOperationType.REMOVE, "oppositeDirection" : true, "depth" : 10 * mm, "offsetDistance" : 25 * mm});
        }
    });
